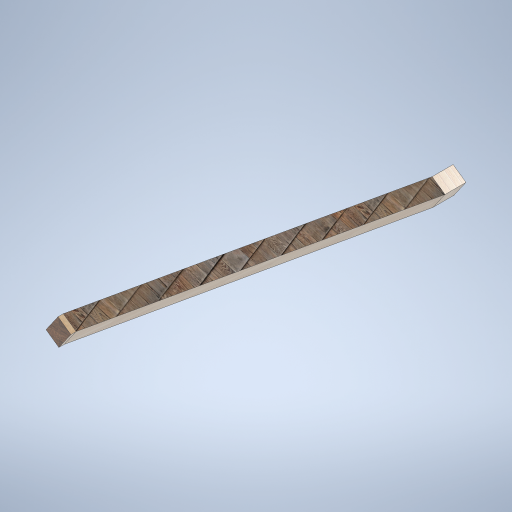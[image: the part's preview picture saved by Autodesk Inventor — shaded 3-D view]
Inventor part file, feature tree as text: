
AUTODESK INVENTOR PART (.ipt)
format: ipt  version: 2024.2 (Build 282272000, 272)  size: 310,784 bytes
history: native  units: mm
features: sketch x4, plane x2, extrude x2, projected_geometry x2, loft x1
ambient origin geometry x8: Origin, YZ Plane, XZ Plane, XY Plane, X Axis, Y Axis, Z Axis, Center Point
bodies: Solid1 (feature_tree)
feature tree (11):
  sketch  "Sketch1"  dims[d0=0.0mm d1=3749.0mm d2=0.0mm d3=90.0deg]
  plane  "Work Plane2"
  loft  "Loft1"
  sketch  "Sketch3"  dims[d8=50.0mm d9=0.0mm]
  sketch  "Sketch4"
  extrude  "Extrusion1"  Depth=200.0mm TaperAngle=0.0deg
  extrude  "Extrusion2"  [1 undecoded]
  plane  "Work Plane1"
  sketch  "Sketch2"  dims[d4=0.0mm d5=90.0deg d6=200.0mm d7=0.0mm]
  projected_geometry  "Projected Loop1"
  projected_geometry  "Projected Loop2"
note: 1 required parameter value undecoded (feature->parameter linkage not recoverable at this tier; creation-order binding heuristic only, values carry confidence <= 0.55)
